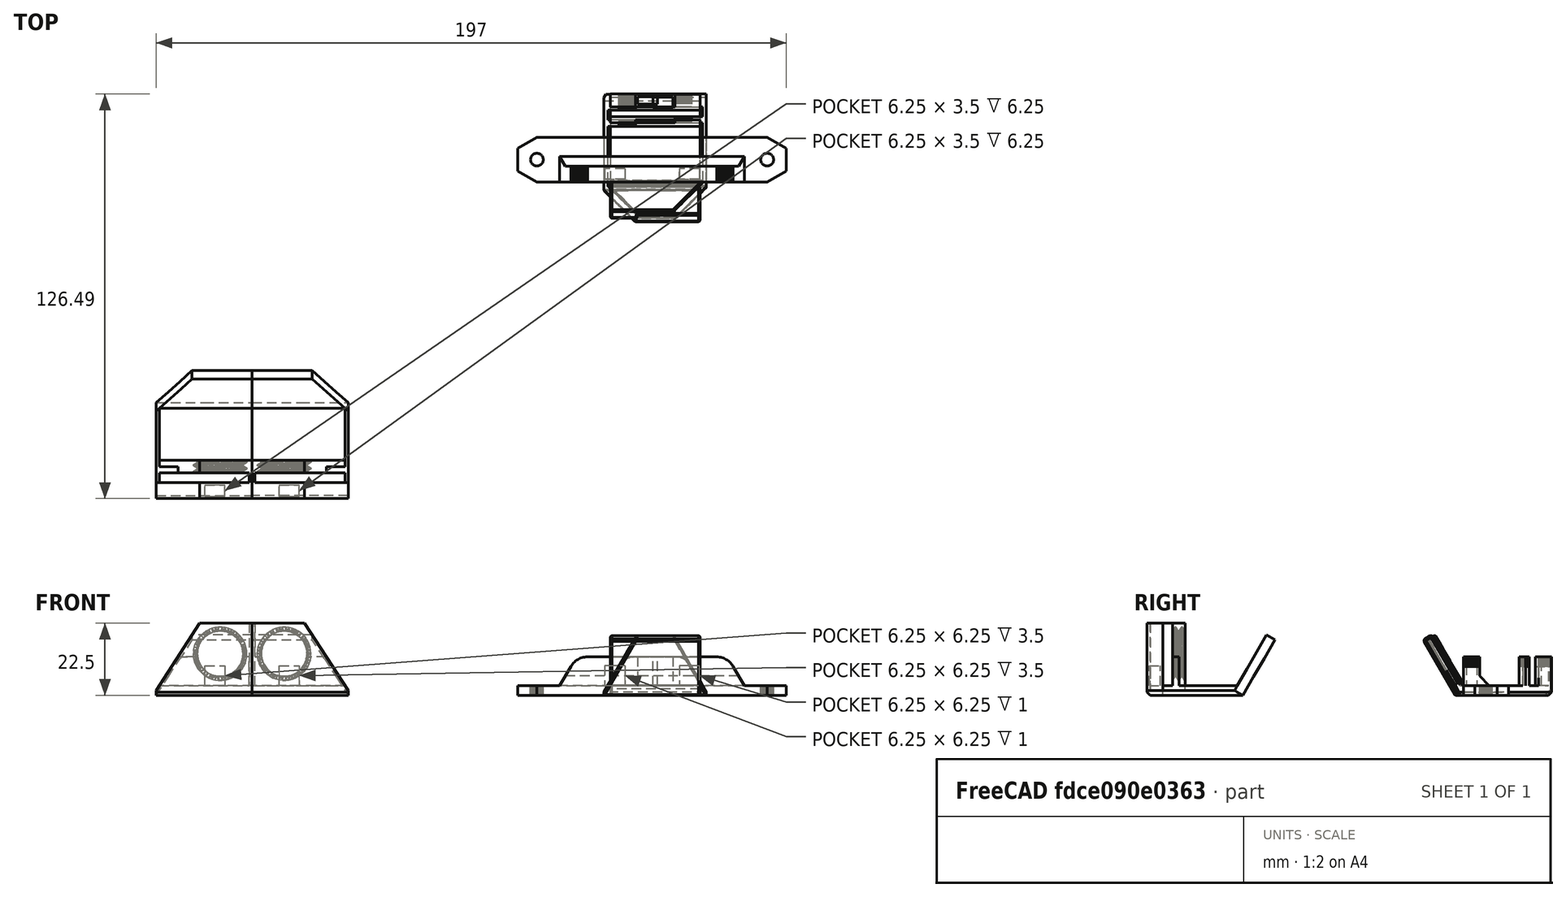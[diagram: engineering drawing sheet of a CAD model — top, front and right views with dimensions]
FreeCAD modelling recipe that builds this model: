
FCSTD DOCUMENT  (FreeCAD 0.20RUnknown)
Label: IkeaLackDoorKnobRemix
License: All rights reserved
LicenseURL: http://en.wikipedia.org/wiki/All_rights_reserved
objects: Sketcher::SketchObject×11, Part::Feature×10, Mesh::Feature×5, PartDesign::Pad×5, PartDesign::Pocket×5, PartDesign::FeatureBase×4, PartDesign::Plane×4, PartDesign::Body×4, PartDesign::Chamfer×2
note: 57 computed .brp shape members not serialized (recipe doc carries the construction recipe); baked Part::Feature solids carry a one-line shape summary decoded from their .brp

FEATURE [Mesh::Feature] inside
FEATURE [Mesh::Feature] left_door_knob  label="left door knob"
FEATURE [Mesh::Feature] right_door_knob  label="right door knob"
FEATURE [Part::Feature] inside001
  shape: bbox 84 x 14 x 12 mm, 584 faces, 0 solids (baked)
FEATURE [Part::Feature] inside001_solid  label="inside001 (Solid)"
  shape: bbox 84 x 14 x 12 mm, 584 faces (baked)
FEATURE [Part::Feature] left_door_knob001
  shape: bbox 30 x 38.82 x 18.64 mm, 2626 faces, 0 solids (baked)
FEATURE [Part::Feature] left_door_knob001_solid  label="left_door_knob001 (Solid)"
  shape: bbox 30 x 38.82 x 18.64 mm, 2626 faces (baked)
FEATURE [Part::Feature] right_door_knob001
  shape: bbox 30 x 38.82 x 18.64 mm, 2626 faces, 0 solids (baked)
FEATURE [Part::Feature] right_door_knob001_solid  label="right_door_knob001 (Solid)"
  shape: bbox 30 x 38.82 x 18.64 mm, 2626 faces (baked)
FEATURE [PartDesign::FeatureBase] BaseFeature
  BaseFeature = -> inside001_solid
FEATURE [PartDesign::Plane] DatumPlane  label="OutsideDatumPlane"
  Length = 211.596
  MapMode = 5
  Placement = pos=(0,102,0) rot=(0,0.707107,0.707107;3.14159rad)
  ResizeMode = 0
  Support = -> [BaseFeature]
  Width = 69.5959
FEATURE [Sketcher::SketchObject] Sketch  label="OutsideSketch"
  ExternalGeometry = -> [BaseFeature]
  FullyConstrained = true
  MapMode = 5
  Placement = pos=(0,102,0) rot=(0,0.707107,0.707107;3.14159rad)
  Support = -> [DatumPlane]
  sketch-geometry (34):
    g0: LineSegment StartX=-151.536 StartY=7 StartZ=0 EndX=-150.381 EndY=9 EndZ=0
    g1: LineSegment StartX=-150.381 StartY=9 StartZ=0 EndX=-150.142 EndY=9.37992 EndZ=0
    g2: LineSegment StartX=-150.142 StartY=9.37992 StartZ=0 EndX=-149.876 EndY=9.74094 EndZ=0
    g3: LineSegment StartX=-149.876 StartY=9.74094 StartZ=0 EndX=-149.583 EndY=10.081 EndZ=0
    g4: LineSegment StartX=-149.583 StartY=10.081 StartZ=0 EndX=-149.266 EndY=10.3983 EndZ=0
    g5: LineSegment StartX=-149.266 StartY=10.3983 StartZ=0 EndX=-148.926 EndY=10.691 EndZ=0
    g6: LineSegment StartX=-148.926 StartY=10.691 StartZ=0 EndX=-148.565 EndY=10.9574 EndZ=0
    g7: LineSegment StartX=-148.565 StartY=10.9574 StartZ=0 EndX=-148.185 EndY=11.1962 EndZ=0
    g8: LineSegment StartX=-148.185 StartY=11.1962 StartZ=0 EndX=-147.788 EndY=11.4058 EndZ=0
    g9: LineSegment StartX=-147.788 StartY=11.4058 StartZ=0 EndX=-147.377 EndY=11.5852 EndZ=0
    g10: LineSegment StartX=-147.377 StartY=11.5852 StartZ=0 EndX=-146.954 EndY=11.7334 EndZ=0
    g11: LineSegment StartX=-146.954 StartY=11.7334 StartZ=0 EndX=-146.52 EndY=11.8496 EndZ=0
    g12: LineSegment StartX=-146.52 StartY=11.8496 StartZ=0 EndX=-146.079 EndY=11.933 EndZ=0
    g13: LineSegment StartX=-146.079 StartY=11.933 StartZ=0 EndX=-145.633 EndY=11.9832 EndZ=0
    g14: LineSegment StartX=-145.633 StartY=11.9832 StartZ=0 EndX=-145.185 EndY=12 EndZ=0
    g15: LineSegment StartX=-145.185 StartY=12 StartZ=0 EndX=-104.815 EndY=12 EndZ=0
    g16: LineSegment StartX=-104.815 StartY=12 StartZ=0 EndX=-104.367 EndY=11.9832 EndZ=0
    g17: LineSegment StartX=-104.367 StartY=11.9832 StartZ=0 EndX=-103.921 EndY=11.933 EndZ=0
    g18: LineSegment StartX=-103.921 StartY=11.933 StartZ=0 EndX=-103.48 EndY=11.8496 EndZ=0
    g19: LineSegment StartX=-103.48 StartY=11.8496 StartZ=0 EndX=-103.046 EndY=11.7334 EndZ=0
    g20: LineSegment StartX=-103.046 StartY=11.7334 StartZ=0 EndX=-102.623 EndY=11.5852 EndZ=0
    g21: LineSegment StartX=-102.623 StartY=11.5852 StartZ=0 EndX=-102.212 EndY=11.4058 EndZ=0
    g22: LineSegment StartX=-102.212 StartY=11.4058 StartZ=0 EndX=-101.815 EndY=11.1962 EndZ=0
    g23: LineSegment StartX=-101.815 StartY=11.1962 StartZ=0 EndX=-101.435 EndY=10.9574 EndZ=0
    g24: LineSegment StartX=-101.435 StartY=10.9574 StartZ=0 EndX=-101.074 EndY=10.691 EndZ=0
    g25: LineSegment StartX=-101.074 StartY=10.691 StartZ=0 EndX=-100.734 EndY=10.3983 EndZ=0
    g26: LineSegment StartX=-100.734 StartY=10.3983 StartZ=0 EndX=-100.417 EndY=10.081 EndZ=0
    g27: LineSegment StartX=-100.417 StartY=10.081 StartZ=0 EndX=-100.124 EndY=9.74094 EndZ=0
    g28: LineSegment StartX=-100.124 StartY=9.74094 StartZ=0 EndX=-99.8575 EndY=9.37992 EndZ=0
    g29: LineSegment StartX=-99.8575 StartY=9.37992 StartZ=0 EndX=-99.6188 EndY=9 EndZ=0
    g30: LineSegment StartX=-99.6188 StartY=9 StartZ=0 EndX=-98.4641 EndY=7 EndZ=0
    g31: LineSegment StartX=-98.4641 StartY=7 StartZ=0 EndX=-96.1547 EndY=3 EndZ=0
    g32: LineSegment StartX=-96.1547 StartY=3 StartZ=0 EndX=-153.845 EndY=3 EndZ=0
    g33: LineSegment StartX=-153.845 StartY=3 StartZ=0 EndX=-151.536 EndY=7 EndZ=0
  constraints (68):
    c: Coincident(g-19,g0)
    c: Coincident(g0,g-18)
    c: Coincident(g0,g1)
    c: Coincident(g1,g-17)
    c: Coincident(g1,g2)
    c: Coincident(g2,g-16)
    c: Coincident(g2,g3)
    c: Coincident(g3,g-15)
    c: Coincident(g3,g4)
    c: Coincident(g4,g-14)
    c: Coincident(g4,g5)
    c: Coincident(g5,g-13)
    c: Coincident(g5,g6)
    c: Coincident(g6,g-12)
    c: Coincident(g6,g7)
    c: Coincident(g7,g-11)
    c: Coincident(g7,g8)
    c: Coincident(g8,g-10)
    c: Coincident(g8,g9)
    c: Coincident(g9,g-9)
    c: Coincident(g9,g10)
    c: Coincident(g10,g-8)
    c: Coincident(g10,g11)
    c: Coincident(g11,g-7)
    c: Coincident(g11,g12)
    c: Coincident(g12,g-6)
    c: Coincident(g12,g13)
    c: Coincident(g13,g-5)
    c: Coincident(g13,g14)
    c: Coincident(g14,g-4)
    c: Coincident(g14,g15)
    c: Coincident(g15,g-20)
    c: Coincident(g15,g16)
    c: Coincident(g16,g-21)
    c: Coincident(g16,g17)
    c: Coincident(g17,g-22)
    c: Coincident(g17,g18)
    c: Coincident(g18,g-23)
    c: Coincident(g18,g19)
    c: Coincident(g19,g-24)
    c: Coincident(g19,g20)
    c: Coincident(g20,g-25)
    c: Coincident(g20,g21)
    c: Coincident(g21,g-26)
    c: Coincident(g21,g22)
    c: Coincident(g22,g-27)
    c: Coincident(g22,g23)
    c: Coincident(g23,g-28)
    c: Coincident(g23,g24)
    c: Coincident(g24,g-29)
    c: Coincident(g24,g25)
    c: Coincident(g25,g-30)
    c: Coincident(g25,g26)
    c: Coincident(g26,g-31)
    c: Coincident(g26,g27)
    c: Coincident(g27,g-32)
    c: Coincident(g27,g28)
    c: Coincident(g28,g-33)
    c: Coincident(g28,g29)
    c: Coincident(g29,g-34)
    c: Coincident(g29,g30)
    c: Coincident(g30,g-35)
    c: Coincident(g30,g31)
    c: Coincident(g31,g-35)
    c: Coincident(g31,g32)
    c: Coincident(g32,g-19)
    c: Coincident(g32,g33)
    c: Coincident(g33,g0)
FEATURE [PartDesign::Pad] Pad
  BaseFeature = -> BaseFeature
  Direction = (0,1,-2e-16)
  Length = 1
  Length2 = 10
  Profile = -> Sketch
  ReferenceAxis = -> Sketch [N_Axis]
  Type = 0
FEATURE [PartDesign::Plane] DatumPlane001  label="InsideDatumPlane"
  Length = 211.596
  MapMode = 5
  Placement = pos=(0,101.125,0) rot=(1,0,0;1.5708rad)
  ResizeMode = 0
  Support = -> [Pad]
  Width = 69.5959
FEATURE [Sketcher::SketchObject] Sketch001  label="InsideSketch"
  ExternalGeometry = -> [Pad]
  FullyConstrained = true
  MapMode = 5
  Placement = pos=(0,101.125,0) rot=(1,0,0;1.5708rad)
  Support = -> [DatumPlane001]
  sketch-geometry (8):
    g0: LineSegment StartX=110.25 StartY=12 StartZ=0 EndX=116.5 EndY=12 EndZ=0
    g1: LineSegment StartX=116.5 StartY=12 StartZ=0 EndX=116.5 EndY=3 EndZ=0
    g2: LineSegment StartX=116.5 StartY=3 StartZ=0 EndX=110.25 EndY=3 EndZ=0
    g3: LineSegment StartX=110.25 StartY=3 StartZ=0 EndX=110.25 EndY=12 EndZ=0
    g4: LineSegment StartX=133.5 StartY=3 StartZ=0 EndX=139.75 EndY=3 EndZ=0
    g5: LineSegment StartX=139.75 StartY=3 StartZ=0 EndX=139.75 EndY=12 EndZ=0
    g6: LineSegment StartX=139.75 StartY=12 StartZ=0 EndX=133.5 EndY=12 EndZ=0
    g7: LineSegment StartX=133.5 StartY=12 StartZ=0 EndX=133.5 EndY=3 EndZ=0
  constraints (20):
    c: Coincident(g0,g1)
    c: Coincident(g1,g2)
    c: Coincident(g2,g3)
    c: Coincident(g3,g0)
    c: Horizontal(g0)
    c: Horizontal(g2)
    c: Vertical(g1)
    c: Vertical(g3)
    c: Coincident(g0,g-4)
    c: Coincident(g1,g-3)
    c: Coincident(g4,g5)
    c: Coincident(g5,g6)
    c: Coincident(g6,g7)
    c: Coincident(g7,g4)
    c: Horizontal(g4)
    c: Horizontal(g6)
    c: Vertical(g5)
    c: Vertical(g7)
    c: Coincident(g4,g-5)
    c: Coincident(g5,g-6)
FEATURE [PartDesign::Pocket] Pocket
  BaseFeature = -> Pad
  Direction = (0,1,-2e-16)
  Length = 1
  Length2 = 5
  Profile = -> Sketch001
  ReferenceAxis = -> Sketch001 [N_Axis]
  Type = 0
FEATURE [PartDesign::FeatureBase] BaseFeature001
  BaseFeature = -> left_door_knob001_solid
FEATURE [PartDesign::Plane] DatumPlane002  label="OutsideDatumPlane001"
  Length = 183.166
  MapMode = 5
  Placement = pos=(0,124.408,0) rot=(0,0.707107,0.707107;3.14159rad)
  ResizeMode = 0
  Support = -> [BaseFeature001]
  Width = 68.1659
FEATURE [Sketcher::SketchObject] Sketch002  label="OutsideSketch001"
  ExternalGeometry = -> [BaseFeature001]
  FullyConstrained = true
  MapMode = 5
  Placement = pos=(0,124.408,0) rot=(0,0.707107,0.707107;3.14159rad)
  Support = -> [DatumPlane002]
  sketch-geometry (22):
    g0: LineSegment StartX=-110 StartY=1 StartZ=0 EndX=-140 EndY=1 EndZ=0
    g1: LineSegment StartX=-140 StartY=1 StartZ=0 EndX=-140 EndY=12 EndZ=0
    g2: LineSegment StartX=-140 StartY=12 StartZ=0 EndX=-119.815 EndY=12 EndZ=0
    g3: LineSegment StartX=-119.815 StartY=12 StartZ=0 EndX=-119.466 EndY=11.9898 EndZ=0
    g4: LineSegment StartX=-119.466 StartY=11.9898 StartZ=0 EndX=-119.118 EndY=11.9594 EndZ=0
    g5: LineSegment StartX=-119.118 StartY=11.9594 StartZ=0 EndX=-118.773 EndY=11.9088 EndZ=0
    g6: LineSegment StartX=-118.773 StartY=11.9088 StartZ=0 EndX=-118.431 EndY=11.8383 EndZ=0
    g7: LineSegment StartX=-118.431 StartY=11.8383 StartZ=0 EndX=-118.094 EndY=11.7479 EndZ=0
    g8: LineSegment StartX=-118.094 StartY=11.7479 StartZ=0 EndX=-117.763 EndY=11.6382 EndZ=0
    g9: LineSegment StartX=-117.763 StartY=11.6382 StartZ=0 EndX=-117.438 EndY=11.5093 EndZ=0
    g10: LineSegment StartX=-117.438 StartY=11.5093 StartZ=0 EndX=-117.122 EndY=11.3618 EndZ=0
    g11: LineSegment StartX=-117.122 StartY=11.3618 StartZ=0 EndX=-116.815 EndY=11.1962 EndZ=0
    g12: LineSegment StartX=-116.815 StartY=11.1962 StartZ=0 EndX=-116.518 EndY=11.0129 EndZ=0
    g13: LineSegment StartX=-116.518 StartY=11.0129 StartZ=0 EndX=-116.232 EndY=10.8127 EndZ=0
    g14: LineSegment StartX=-116.232 StartY=10.8127 StartZ=0 EndX=-115.958 EndY=10.5963 EndZ=0
    g15: LineSegment StartX=-115.958 StartY=10.5963 StartZ=0 EndX=-115.697 EndY=10.3642 EndZ=0
    g16: LineSegment StartX=-115.697 StartY=10.3642 StartZ=0 EndX=-115.451 EndY=10.1174 EndZ=0
    g17: LineSegment StartX=-115.451 StartY=10.1174 StartZ=0 EndX=-115.219 EndY=9.85673 EndZ=0
    g18: LineSegment StartX=-115.219 StartY=9.85673 StartZ=0 EndX=-115.002 EndY=9.58295 EndZ=0
    g19: LineSegment StartX=-115.002 StartY=9.58295 StartZ=0 EndX=-114.802 EndY=9.29705 EndZ=0
    g20: LineSegment StartX=-114.802 StartY=9.29705 StartZ=0 EndX=-114.619 EndY=9 EndZ=0
    g21: LineSegment StartX=-114.619 StartY=9 StartZ=0 EndX=-110 EndY=1 EndZ=0
  constraints (44):
    c: Coincident(g-6,g0)
    c: Coincident(g0,g-5)
    c: Coincident(g0,g1)
    c: Coincident(g1,g-4)
    c: Coincident(g1,g2)
    c: Coincident(g2,g-24)
    c: Coincident(g2,g3)
    c: Coincident(g3,g-24)
    c: Coincident(g3,g4)
    c: Coincident(g4,g-23)
    c: Coincident(g4,g5)
    c: Coincident(g5,g-22)
    c: Coincident(g5,g6)
    c: Coincident(g6,g-21)
    c: Coincident(g6,g7)
    c: Coincident(g7,g-20)
    c: Coincident(g7,g8)
    c: Coincident(g8,g-19)
    c: Coincident(g8,g9)
    c: Coincident(g9,g-18)
    c: Coincident(g9,g10)
    c: Coincident(g10,g-17)
    c: Coincident(g10,g11)
    c: Coincident(g11,g-16)
    c: Coincident(g11,g12)
    c: Coincident(g12,g-15)
    c: Coincident(g12,g13)
    c: Coincident(g13,g-14)
    c: Coincident(g13,g14)
    c: Coincident(g14,g-13)
    c: Coincident(g14,g15)
    c: Coincident(g15,g-12)
    c: Coincident(g15,g16)
    c: Coincident(g16,g-11)
    c: Coincident(g16,g17)
    c: Coincident(g17,g-10)
    c: Coincident(g17,g18)
    c: Coincident(g18,g-9)
    c: Coincident(g18,g19)
    c: Coincident(g19,g-8)
    c: Coincident(g19,g20)
    c: Coincident(g20,g-7)
    c: Coincident(g20,g21)
    c: Coincident(g21,g0)
FEATURE [PartDesign::Pad] Pad001
  BaseFeature = -> BaseFeature001
  Direction = (0,1,-2e-16)
  Length = 1
  Length2 = 10
  Profile = -> Sketch002
  ReferenceAxis = -> Sketch002 [N_Axis]
  Type = 0
FEATURE [PartDesign::Plane] DatumPlane003  label="InsideDatumPlane001"
  Length = 183.166
  MapMode = 5
  Placement = pos=(0,123.533,0) rot=(1,0,0;1.5708rad)
  ResizeMode = 0
  Support = -> [Pad001]
  Width = 68.1659
FEATURE [Sketcher::SketchObject] Sketch003  label="InsideSketch001"
  ExternalGeometry = -> [Pad001]
  FullyConstrained = true
  MapMode = 5
  Placement = pos=(0,123.533,0) rot=(1,0,0;1.5708rad)
  Support = -> [DatumPlane003]
  sketch-geometry (4):
    g0: LineSegment StartX=125.25 StartY=12 StartZ=0 EndX=131.5 EndY=12 EndZ=0
    g1: LineSegment StartX=131.5 StartY=12 StartZ=0 EndX=131.5 EndY=3 EndZ=0
    g2: LineSegment StartX=131.5 StartY=3 StartZ=0 EndX=125.25 EndY=3 EndZ=0
    g3: LineSegment StartX=125.25 StartY=3 StartZ=0 EndX=125.25 EndY=12 EndZ=0
  constraints (10):
    c: Coincident(g0,g1)
    c: Coincident(g1,g2)
    c: Coincident(g2,g3)
    c: Coincident(g3,g0)
    c: Horizontal(g0)
    c: Horizontal(g2)
    c: Vertical(g1)
    c: Vertical(g3)
    c: Coincident(g0,g-4)
    c: Coincident(g1,g-3)
FEATURE [PartDesign::Pocket] Pocket001
  BaseFeature = -> Pad001
  Direction = (0,1,-2e-16)
  Length = 1
  Length2 = 5
  Profile = -> Sketch003
  ReferenceAxis = -> Sketch003 [N_Axis]
  Type = 0
FEATURE [Sketcher::SketchObject] Sketch004
  ExternalGeometry = -> [Pocket001]
  FullyConstrained = true
  MapMode = 5
  Placement = pos=(0,61.7042,-61.7042) rot=(1,0,0;3.92699rad)
  Support = -> [Pocket001]
  sketch-geometry (4):
    g0: LineSegment StartX=140 StartY=-87.263 StartZ=0 EndX=110 EndY=-87.263 EndZ=0
    g1: LineSegment StartX=110 StartY=-87.263 StartZ=0 EndX=110 EndY=-92.263 EndZ=0
    g2: LineSegment StartX=110 StartY=-92.263 StartZ=0 EndX=140 EndY=-92.263 EndZ=0
    g3: LineSegment StartX=140 StartY=-92.263 StartZ=0 EndX=140 EndY=-87.263 EndZ=0
  constraints (10):
    c: Coincident(g0,g1)
    c: Coincident(g1,g2)
    c: Coincident(g2,g3)
    c: Coincident(g3,g0)
    c: Coincident(g0,g-4)
    c: Coincident(g-3,g0)
    c: Vertical(g1)
    c: Vertical(g3)
    c: DistanceY(g3,g3) = 5
    c: Horizontal(g2)
FEATURE [PartDesign::Pocket] Pocket002  label="ManualChamfer"
  BaseFeature = -> Pocket001
  Direction = (0,-0.707107,0.707107)
  Length = 5
  Length2 = 5
  Profile = -> Sketch004
  ReferenceAxis = -> Sketch004 [N_Axis]
  Reversed = true
  Type = 0
FEATURE [Sketcher::SketchObject] Sketch005
  ExternalGeometry = -> [Pocket]
  FullyConstrained = true
  MapMode = 5
  Placement = pos=(0,102.125,0) rot=(1,0,0;1.5708rad)
  Support = -> [Pocket]
  sketch-geometry (16):
    g0: LineSegment StartX=110.25 StartY=3 StartZ=0 EndX=116.5 EndY=3 EndZ=0
    g1: LineSegment StartX=116.5 StartY=3 StartZ=0 EndX=116.5 EndY=9.25 EndZ=0
    g2: LineSegment StartX=116.5 StartY=9.25 StartZ=0 EndX=110.25 EndY=9.25 EndZ=0
    g3: LineSegment StartX=110.25 StartY=9.25 StartZ=0 EndX=110.25 EndY=3 EndZ=0
    g4: LineSegment StartX=133.5 StartY=3 StartZ=0 EndX=139.75 EndY=3 EndZ=0
    g5: LineSegment StartX=139.75 StartY=3 StartZ=0 EndX=139.75 EndY=9.25 EndZ=0
    g6: LineSegment StartX=139.75 StartY=9.25 StartZ=0 EndX=133.5 EndY=9.25 EndZ=0
    g7: LineSegment StartX=133.5 StartY=9.25 StartZ=0 EndX=133.5 EndY=3 EndZ=0
    g8: LineSegment StartX=110.25 StartY=12 StartZ=0 EndX=116.5 EndY=12 EndZ=0
    g9: LineSegment StartX=116.5 StartY=12 StartZ=0 EndX=116.5 EndY=9.25 EndZ=0
    g10: LineSegment StartX=116.5 StartY=9.25 StartZ=0 EndX=110.25 EndY=9.25 EndZ=0
    g11: LineSegment StartX=110.25 StartY=9.25 StartZ=0 EndX=110.25 EndY=12 EndZ=0
    g12: LineSegment StartX=133.5 StartY=12 StartZ=0 EndX=139.75 EndY=12 EndZ=0
    g13: LineSegment StartX=139.75 StartY=12 StartZ=0 EndX=139.75 EndY=9.25 EndZ=0
    g14: LineSegment StartX=139.75 StartY=9.25 StartZ=0 EndX=133.5 EndY=9.25 EndZ=0
    g15: LineSegment StartX=133.5 StartY=9.25 StartZ=0 EndX=133.5 EndY=12 EndZ=0
  constraints (42):
    c: Coincident(g0,g1)
    c: Coincident(g1,g2)
    c: Coincident(g2,g3)
    c: Coincident(g3,g0)
    c: Horizontal(g0)
    c: Horizontal(g2)
    c: Vertical(g1)
    c: Vertical(g3)
    c: Coincident(g0,g-6)
    c: PointOnObject(g1,g-5)
    c: Coincident(g4,g5)
    c: Coincident(g5,g6)
    c: Coincident(g6,g7)
    c: Coincident(g7,g4)
    c: Horizontal(g4)
    c: Horizontal(g6)
    c: Vertical(g5)
    c: Vertical(g7)
    c: Coincident(g4,g-4)
    c: PointOnObject(g5,g-3)
    c: Equal(g2,g3)
    c: Equal(g7,g6)
    c: Coincident(g8,g9)
    c: Coincident(g9,g10)
    c: Coincident(g10,g11)
    c: Coincident(g11,g8)
    c: Horizontal(g8)
    c: Horizontal(g10)
    c: Vertical(g9)
    c: Vertical(g11)
    c: Coincident(g8,g-6)
    c: Coincident(g9,g1)
    c: Coincident(g12,g13)
    c: Coincident(g13,g14)
    c: Coincident(g14,g15)
    c: Coincident(g15,g12)
    c: Horizontal(g12)
    c: Horizontal(g14)
    c: Vertical(g13)
    c: Vertical(g15)
    c: Coincident(g12,g-4)
    c: Coincident(g13,g5)
FEATURE [PartDesign::Pad] Pad002  label="PadClosed"
  BaseFeature = -> Pocket
  Direction = (0,-1,2e-16)
  Length = 10
  Length2 = 10
  Profile = -> Sketch005
  ReferenceAxis = -> Sketch005 [N_Axis]
  Type = 2
FEATURE [PartDesign::Body] Body  label="Inside"
  BaseFeature = -> inside001_solid
  Group = -> [BaseFeature,DatumPlane,Sketch,Pad,DatumPlane001,Sketch001,Pocket,Sketch005,Pad002]
  Origin = -> Origin
  Tip = -> Pad002
FEATURE [Mesh::Feature] knob_left  label="knob-left"
FEATURE [Part::Feature] knob_left001
  shape: bbox 30 x 39 x 22.5 mm, 6500 faces, 0 solids (baked)
FEATURE [Part::Feature] knob_left001_solid  label="knob_left001 (Solid)"
  shape: bbox 30 x 39 x 22.5 mm, 6500 faces (baked)
FEATURE [PartDesign::FeatureBase] BaseFeature002
  BaseFeature = -> knob_left001_solid
FEATURE [Sketcher::SketchObject] Sketch006  label="dim"
  ExternalGeometry = -> [Pocket002]
  FullyConstrained = true
  MapMode = 5
  Placement = pos=(0,124.533,0) rot=(1,0,0;1.5708rad)
  Support = -> [Pocket002]
  constraints (2):
    c: DistanceY(g-3,g-4) = 3  'pad_bottom'
    c: DistanceX(g-4,g-3) = 8.5  'pad_right'
FEATURE [PartDesign::Body] Body001  label="LeftDoorKnob"
  BaseFeature = -> left_door_knob001_solid
  Group = -> [BaseFeature001,DatumPlane002,Sketch002,Pad001,DatumPlane003,Sketch003,Pocket001,Sketch004,Pocket002,Sketch006]
  Origin = -> Origin001
  Tip = -> Pocket002
FEATURE [Sketcher::SketchObject] Sketch007
  ExternalGeometry = -> [BaseFeature002]
  FullyConstrained = true
  MapMode = 5
  Placement = pos=(0,4,0) rot=(0,0.707107,0.707107;3.14159rad)
  Support = -> [BaseFeature002]
  sketch-geometry (5):
    g0: LineSegment StartX=-16.4004 StartY=22.5 StartZ=0 EndX=-30.0017 EndY=1.5 EndZ=0
    g1: LineSegment StartX=-30.0017 StartY=1.5 StartZ=0 EndX=-30.0017 EndY=-9e-16 EndZ=0
    g2: LineSegment StartX=-30.0017 StartY=-9e-16 StartZ=0 EndX=-0.00166988 EndY=-7e-16 EndZ=0
    g3: LineSegment StartX=-0.00166988 StartY=-7e-16 StartZ=0 EndX=0 EndY=22.5 EndZ=0
    g4: LineSegment StartX=0 StartY=22.5 StartZ=0 EndX=-16.4004 EndY=22.5 EndZ=0
  constraints (10):
    c: Coincident(g-3,g0)
    c: Coincident(g0,g1)
    c: Coincident(g1,g-6)
    c: Coincident(g1,g2)
    c: Coincident(g2,g-5)
    c: Coincident(g2,g3)
    c: Coincident(g3,g-4)
    c: Coincident(g3,g4)
    c: Coincident(g4,g0)
    c: Coincident(g-7,g0)
FEATURE [PartDesign::Pad] Pad003
  BaseFeature = -> BaseFeature002
  Direction = (0,1,-2e-16)
  Length = 5
  Length2 = 10
  Profile = -> Sketch007
  ReferenceAxis = -> Sketch007 [N_Axis]
  Reversed = true
  Type = 0
FEATURE [PartDesign::Chamfer] Chamfer
  Angle = 45
  Base = -> Pad003 [Edge23]
  BaseFeature = -> Pad003
  ChamferType = 0
  FlipDirection = false
  Size = 1
  Size2 = 1
  SupportTransform = false
  UseAllEdges = false
FEATURE [Sketcher::SketchObject] Sketch008
  AttachmentOffset = pos=(0,0,-2.5) rot=(0,0,1;0rad)
  FullyConstrained = true
  MapMode = 5
  Placement = pos=(0,1.5,-3e-16) rot=(1,0,0;1.5708rad)
  Support = -> [Chamfer]
  sketch-geometry (4):
    g0: LineSegment StartX=8.5 StartY=9.25 StartZ=0 EndX=14.75 EndY=9.25 EndZ=0
    g1: LineSegment StartX=14.75 StartY=9.25 StartZ=0 EndX=14.75 EndY=3 EndZ=0
    g2: LineSegment StartX=14.75 StartY=3 StartZ=0 EndX=8.5 EndY=3 EndZ=0
    g3: LineSegment StartX=8.5 StartY=3 StartZ=0 EndX=8.5 EndY=9.25 EndZ=0
  constraints (12):
    c: Coincident(g0,g1)
    c: Coincident(g1,g2)
    c: Coincident(g2,g3)
    c: Coincident(g3,g0)
    c: Horizontal(g0)
    c: Horizontal(g2)
    c: Vertical(g1)
    c: Vertical(g3)
    c: Equal(g0,g3)
    c: DistanceX(g0,g0) = 6.25
    c: DistanceX(g-1,g2) = 8.5
    c: DistanceY(g-1,g2) = 3
FEATURE [PartDesign::Pocket] Pocket003
  BaseFeature = -> Chamfer
  Direction = (0,1,-2e-16)
  Length = 3.5
  Length2 = 5
  Midplane = true
  Profile = -> Sketch008
  ReferenceAxis = -> Sketch008 [N_Axis]
  Type = 0
FEATURE [PartDesign::Body] Body002  label="knob-left-thread"
  BaseFeature = -> knob_left001_solid
  Group = -> [BaseFeature002,Sketch007,Pad003,Chamfer,Sketch008,Pocket003]
  Origin = -> Origin002
  Tip = -> Pocket003
FEATURE [Mesh::Feature] knob_right  label="knob-right"
FEATURE [Part::Feature] knob_right001
  shape: bbox 30 x 39 x 22.5 mm, 6511 faces, 0 solids (baked)
FEATURE [Part::Feature] knob_right001_solid  label="knob_right001 (Solid)"
  shape: bbox 30 x 39 x 22.5 mm, 6511 faces (baked)
FEATURE [PartDesign::FeatureBase] BaseFeature003
  BaseFeature = -> knob_right001_solid
FEATURE [Sketcher::SketchObject] Sketch009
  ExternalGeometry = -> [BaseFeature003]
  FullyConstrained = true
  MapMode = 5
  Placement = pos=(0,4,0) rot=(0,0.707107,0.707107;3.14159rad)
  Support = -> [BaseFeature003]
  sketch-geometry (5):
    g0: LineSegment StartX=-1e-16 StartY=22.5 StartZ=0 EndX=16.4004 EndY=22.5 EndZ=0
    g1: LineSegment StartX=16.4004 StartY=22.5 StartZ=0 EndX=30.0017 EndY=1.5 EndZ=0
    g2: LineSegment StartX=30.0017 StartY=1.5 StartZ=0 EndX=30.0017 EndY=-7e-16 EndZ=0
    g3: LineSegment StartX=30.0017 StartY=-7e-16 StartZ=0 EndX=0 EndY=0 EndZ=0
    g4: LineSegment StartX=0 StartY=0 StartZ=0 EndX=-1e-16 EndY=22.5 EndZ=0
  constraints (10):
    c: Coincident(g-5,g0)
    c: Coincident(g0,g-3)
    c: Coincident(g0,g1)
    c: Coincident(g1,g-4)
    c: Coincident(g1,g2)
    c: Coincident(g2,g-4)
    c: Coincident(g2,g3)
    c: Coincident(g3,g-1)
    c: Coincident(g3,g4)
    c: Coincident(g4,g0)
FEATURE [PartDesign::Pad] Pad004
  BaseFeature = -> BaseFeature003
  Direction = (0,1,-2e-16)
  Length = 5
  Length2 = 10
  Profile = -> Sketch009
  ReferenceAxis = -> Sketch009 [N_Axis]
  Reversed = true
  Type = 0
FEATURE [PartDesign::Chamfer] Chamfer001
  Angle = 45
  Base = -> Pad004 [Edge8]
  BaseFeature = -> Pad004
  ChamferType = 0
  FlipDirection = false
  Size = 1
  Size2 = 1
  SupportTransform = false
  UseAllEdges = false
FEATURE [Sketcher::SketchObject] Sketch010
  AttachmentOffset = pos=(0,0,-2.5) rot=(0,0,1;0rad)
  FullyConstrained = true
  MapMode = 5
  Placement = pos=(0,1.5,-3e-16) rot=(1,0,0;1.5708rad)
  Support = -> [Chamfer001]
  sketch-geometry (4):
    g0: LineSegment StartX=-14.75 StartY=9.25 StartZ=0 EndX=-8.5 EndY=9.25 EndZ=0
    g1: LineSegment StartX=-8.5 StartY=9.25 StartZ=0 EndX=-8.5 EndY=3 EndZ=0
    g2: LineSegment StartX=-8.5 StartY=3 StartZ=0 EndX=-14.75 EndY=3 EndZ=0
    g3: LineSegment StartX=-14.75 StartY=3 StartZ=0 EndX=-14.75 EndY=9.25 EndZ=0
  constraints (12):
    c: Coincident(g0,g1)
    c: Coincident(g1,g2)
    c: Coincident(g2,g3)
    c: Coincident(g3,g0)
    c: Horizontal(g0)
    c: Horizontal(g2)
    c: Vertical(g1)
    c: Vertical(g3)
    c: Equal(g0,g1)
    c: DistanceX(g0,g0) = 6.25
    c: DistanceX(g1,g-1) = 8.5
    c: DistanceY(g-1,g1) = 3
FEATURE [PartDesign::Pocket] Pocket004
  BaseFeature = -> Chamfer001
  Direction = (0,1,-2e-16)
  Length = 3.5
  Length2 = 5
  Midplane = true
  Profile = -> Sketch010
  ReferenceAxis = -> Sketch010 [N_Axis]
  Type = 0
FEATURE [PartDesign::Body] Body003  label="knob-right-thread"
  BaseFeature = -> knob_right001_solid
  Group = -> [BaseFeature003,Sketch009,Pad004,Chamfer001,Sketch010,Pocket004]
  Origin = -> Origin003
  Tip = -> Pocket004
